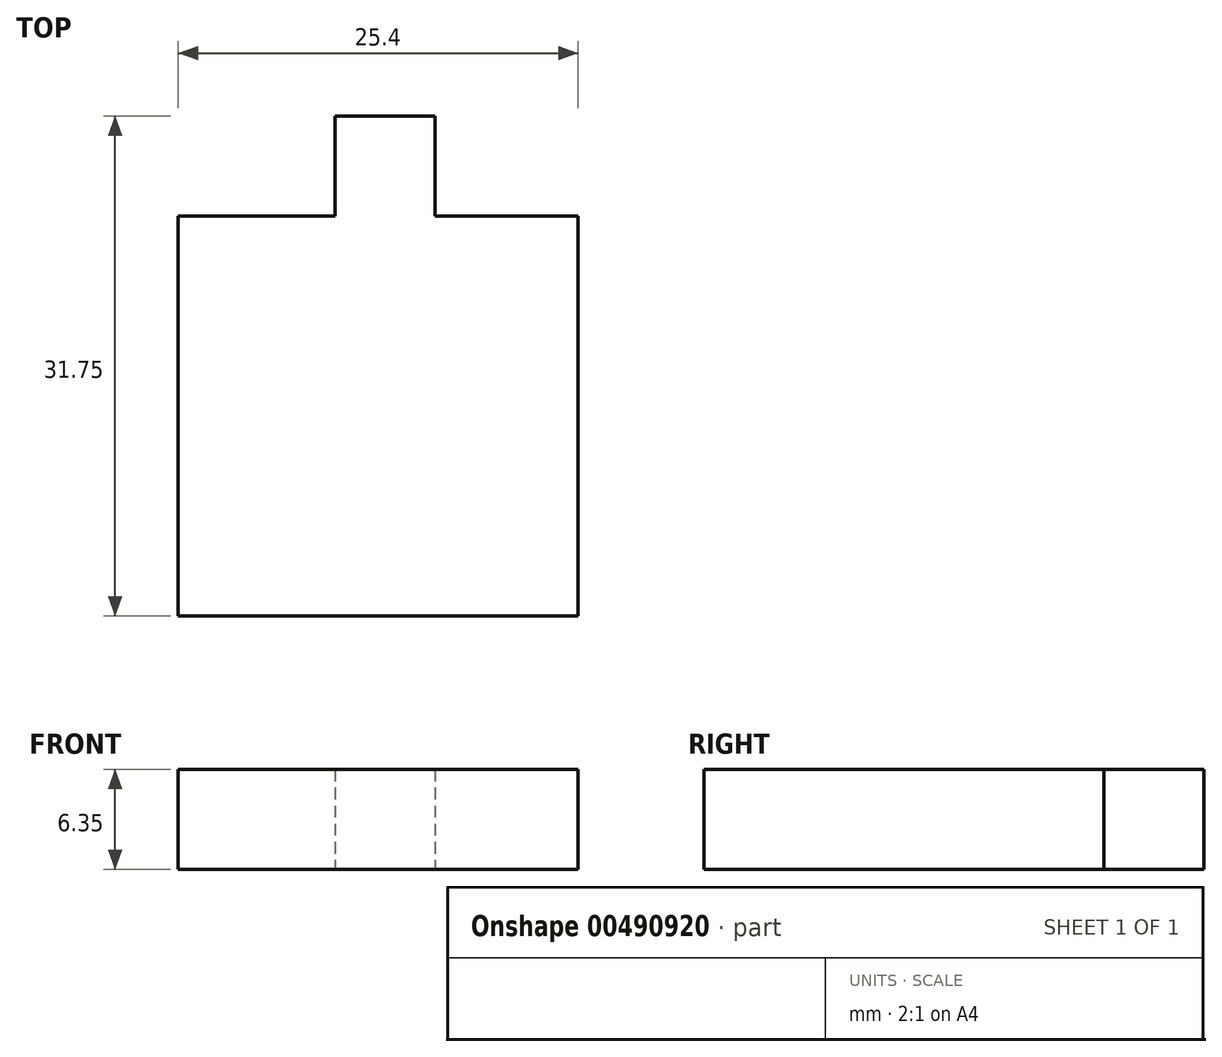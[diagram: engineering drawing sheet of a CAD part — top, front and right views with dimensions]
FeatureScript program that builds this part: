
annotation { "Feature Type Name" : "Feature", "Feature Type Description" : "" }
export const myFeature = defineFeature(function(context is Context, id is Id, definition is map)
    precondition{}
    {
        {
            var Q0;
            Q0=qCreatedBy(makeId("Top.planeOp"),FACE);
            var sketch = newSketch(context, id + "F0", { "sketchPlane" : qUnion([Q0])});
            skLineSegment(sketch, "E0", {"start": v(0, 0) * mm, "end": v(25.4, 0) * mm});
            skLineSegment(sketch, "E1", {"start": v(25.4, 0) * mm, "end": v(25.4, 25.4) * mm});
            skLineSegment(sketch, "E2", {"start": v(25.4, 25.4) * mm, "end": v(16.33, 25.4) * mm});
            skLineSegment(sketch, "E3", {"start": v(16.33, 25.4) * mm, "end": v(16.33, 31.75) * mm});
            skLineSegment(sketch, "E4", {"start": v(16.33, 31.75) * mm, "end": v(9.98, 31.75) * mm});
            skLineSegment(sketch, "E5", {"start": v(9.98, 31.75) * mm, "end": v(9.98, 25.4) * mm});
            skLineSegment(sketch, "E6", {"start": v(9.98, 25.4) * mm, "end": v(0, 25.4) * mm});
            skLineSegment(sketch, "E7", {"start": v(0, 25.4) * mm, "end": v(0, 0) * mm});
            skSolve(sketch);
        }
        {
            var Q0;
            Q0 = qSketchRegion(id + "F0", true);
            extrude(context, id + "F1", {"entities" : qUnion([Q0]), "depth" : 6.35 * mm});
        }
    });
